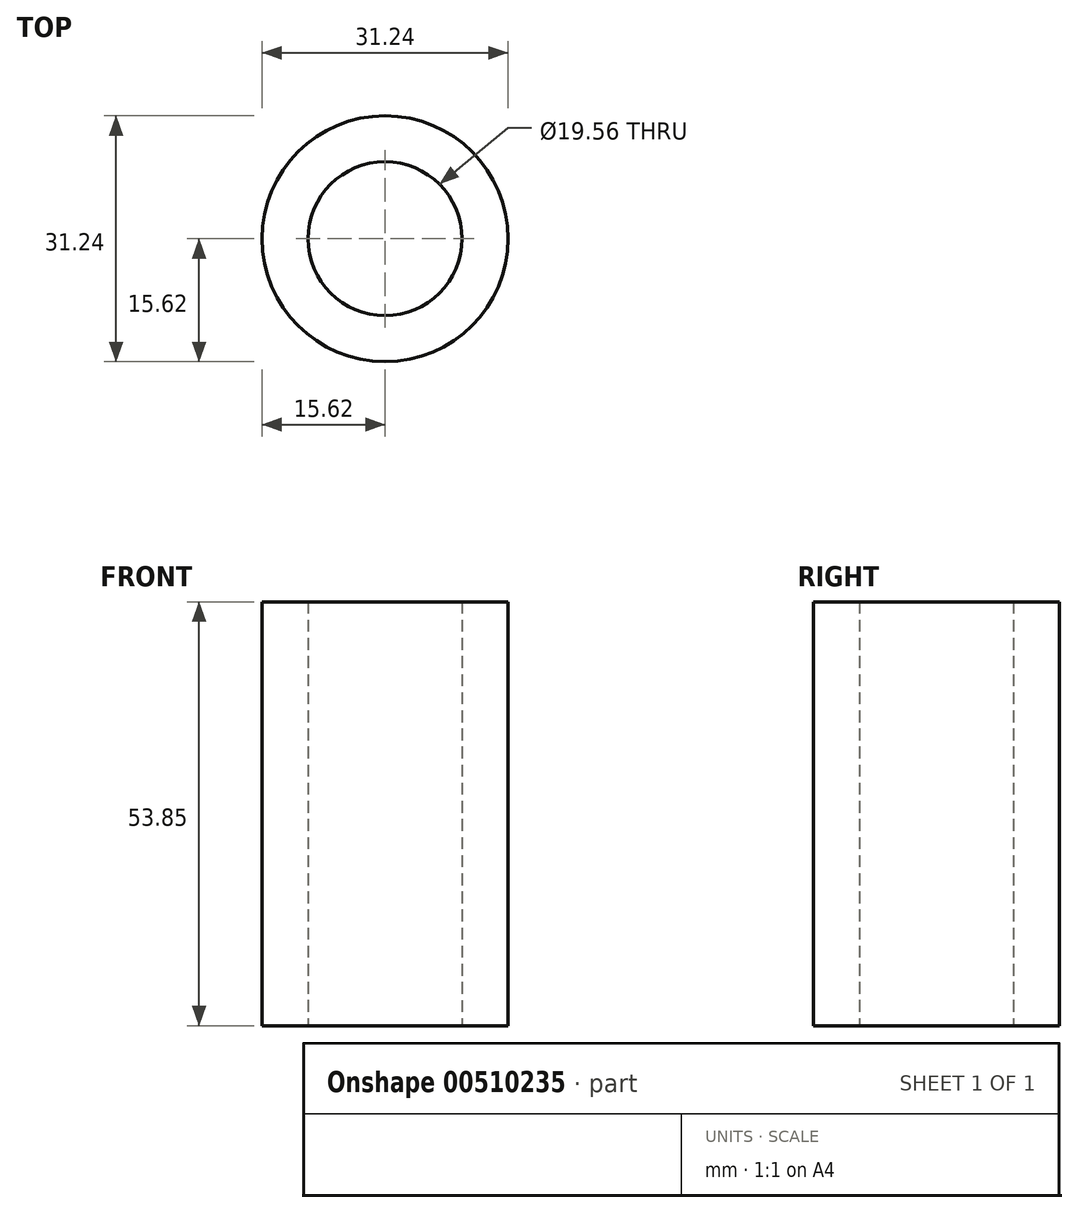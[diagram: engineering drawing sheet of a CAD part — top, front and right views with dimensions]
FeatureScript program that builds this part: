
annotation { "Feature Type Name" : "Feature", "Feature Type Description" : "" }
export const myFeature = defineFeature(function(context is Context, id is Id, definition is map)
    precondition{}
    {
        {
            var Q0;
            Q0=qCreatedBy(makeId("Top.planeOp"),FACE);
            var sketch = newSketch(context, id + "F0", { "sketchPlane" : qUnion([Q0])});
            skCircle(sketch, "E0", {"center": v(0, 0) * mm, "radius": 9.78 * mm});
            skCircle(sketch, "E1", {"center": v(0, 0) * mm, "radius": 15.62 * mm});
            skSolve(sketch);
        }
        {
            var Q0;
            Q0=makeQuery(id+"F0.imprint","IMPRINT",FACE,{"disambiguationData":[TD([[makeQuery(id+"F0.imprint","IMPRINT",EDGE,{"derivedFrom":sQuery(id+"F0.wireOp",EDGE,"E0")}),-1.0]])]});
            extrude(context, id + "F1", {"entities" : qUnion([Q0]), "depth" : 53.85 * mm});
        }
    });
